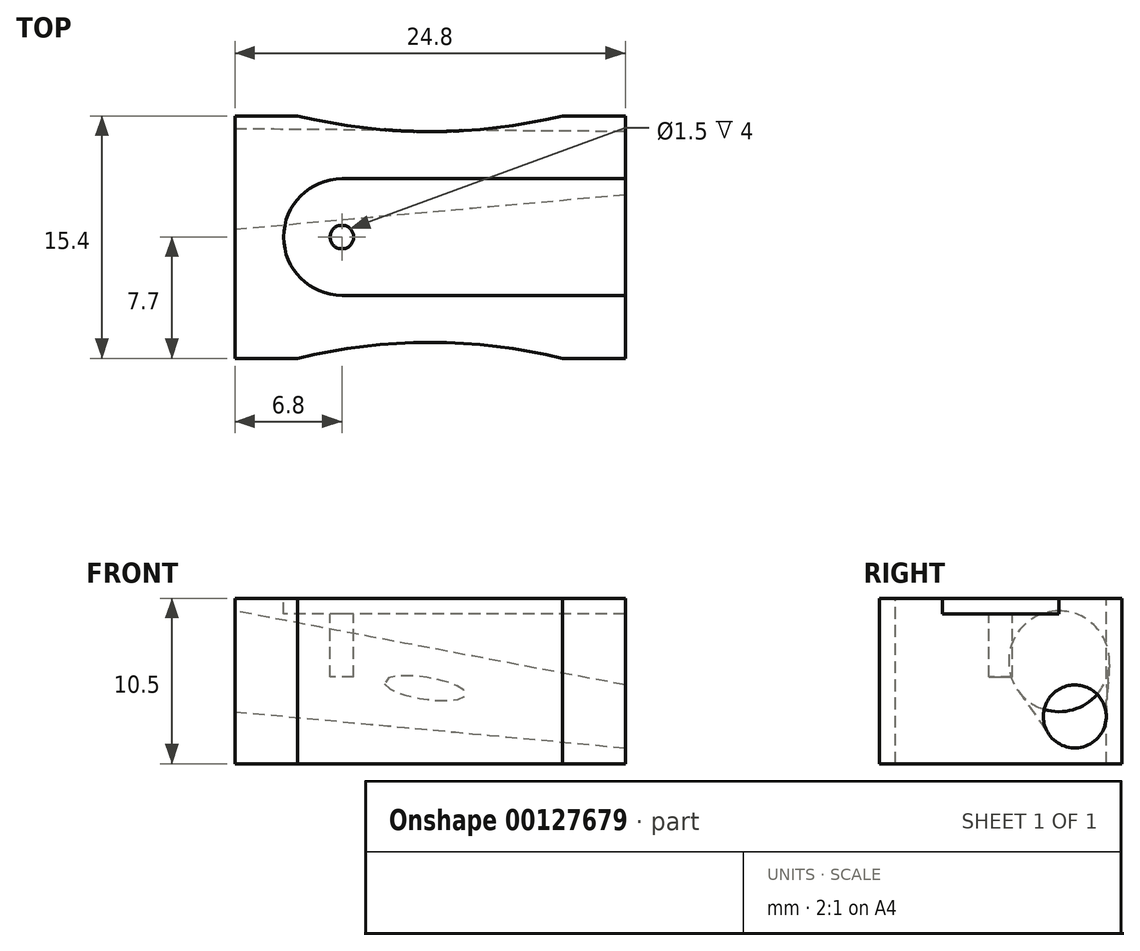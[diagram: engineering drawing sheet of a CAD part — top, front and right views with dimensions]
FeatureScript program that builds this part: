
annotation { "Feature Type Name" : "Feature", "Feature Type Description" : "" }
export const myFeature = defineFeature(function(context is Context, id is Id, definition is map)
    precondition{}
    {
        {
            var Q0;
            Q0=qCreatedBy(makeId("Top.planeOp"),FACE);
            var sketch = newSketch(context, id + "F0", { "sketchPlane" : qUnion([Q0])});
            skLineSegment(sketch, "E0.bottom", {"start": v(0, 0) * mm, "end": v(24.8, 0) * mm});
            skLineSegment(sketch, "E0.top", {"start": v(0, 15.4) * mm, "end": v(24.8, 15.4) * mm});
            skLineSegment(sketch, "E0.left", {"start": v(0, 0) * mm, "end": v(0, 15.4) * mm});
            skLineSegment(sketch, "E0.right", {"start": v(24.8, 0) * mm, "end": v(24.8, 15.4) * mm});
            skSolve(sketch);
        }
        {
            var Q0;
            Q0=makeQuery(id+"F0.imprint","IMPRINT",FACE,{"disambiguationData":[TD([[makeQuery(id+"F0.imprint","IMPRINT",EDGE,{"derivedFrom":sQuery(id+"F0.wireOp",EDGE,"E0.bottom")}),1.0]])]});
            extrude(context, id + "F1", {"entities" : qUnion([Q0]), "depth" : 10.5 * mm});
        }
        {
            var Q0;
            Q0=makeQuery(id+"F1.opExtrude","CAP_FACE",FACE,{"disambiguationData":[OSD([sQuery(id+"F0.wireOp",EDGE,"E0.bottom"),sQuery(id+"F0.wireOp",EDGE,"E0.top"),sQuery(id+"F0.wireOp",EDGE,"E0.left"),sQuery(id+"F0.wireOp",EDGE,"E0.right")])],"isStart":false});
            var sketch = newSketch(context, id + "F2", { "sketchPlane" : qUnion([Q0])});
            skLineSegment(sketch, "E1", {"start": v(24.8, 11.4) * mm, "end": v(6.8, 11.4) * mm});
            skLineSegment(sketch, "E2", {"start": v(24.8, 4) * mm, "end": v(6.8, 4) * mm});
            skArc(sketch, "E3", {"start": v(6.8, 11.4) * mm, "mid": v(3.1, 7.7) * mm, "end": v(6.8, 4) * mm});
            skSolve(sketch);
        }
        {
            var Q0;
            {var subQ0=sQuery(id+"F2.wireOp",EDGE,"E1");Q0=makeQuery(id+"F2.imprint","IMPRINT",FACE,{"disambiguationData":[TD([[makeQuery(id+"F2.imprint","IMPRINT",EDGE,{"derivedFrom":subQ0}),1.0]])]});}
            extrude(context, id + "F3", {"entities" : qUnion([Q0]), "operationType" : NewBodyOperationType.REMOVE, "oppositeDirection" : true, "depth" : 1 * mm});
        }
        {
            var Q0;
            Q0=makeQuery(id+"F1.opExtrude","CAP_FACE",FACE,{"disambiguationData":[OSD([sQuery(id+"F0.wireOp",EDGE,"E0.bottom"),sQuery(id+"F0.wireOp",EDGE,"E0.top"),sQuery(id+"F0.wireOp",EDGE,"E0.left"),sQuery(id+"F0.wireOp",EDGE,"E0.right")])],"isStart":false});
            var sketch = newSketch(context, id + "F4", { "sketchPlane" : qUnion([Q0])});
            skArc(sketch, "E4", {"start": v(4, 15.4) * mm, "mid": v(12.4, 14.4) * mm, "end": v(20.8, 15.4) * mm});
            skArc(sketch, "E5", {"start": v(20.8, 0) * mm, "mid": v(12.4, 1) * mm, "end": v(4, 0) * mm});
            skSolve(sketch);
        }
        {
            var Q0;
            {var subQ0=sQuery(id+"F4.wireOp",EDGE,"E4");Q0=makeQuery(id+"F4.imprint","IMPRINT",FACE,{"disambiguationData":[TD([[makeQuery(id+"F4.imprint","IMPRINT",EDGE,{"derivedFrom":subQ0}),1.0]])]});}
            var Q1;
            {var subQ0=sQuery(id+"F4.wireOp",EDGE,"E5");Q1=makeQuery(id+"F4.imprint","IMPRINT",FACE,{"disambiguationData":[TD([[makeQuery(id+"F4.imprint","IMPRINT",EDGE,{"derivedFrom":subQ0}),1.0]])]});}
            extrude(context, id + "F5", {"entities" : qUnion([Q0, Q1]), "operationType" : NewBodyOperationType.REMOVE, "oppositeDirection" : true, "depth" : 25 * mm});
        }
        {
            var Q0;
            Q0=makeQuery(id+"F1.opExtrude","SWEPT_FACE",FACE,{"disambiguationData":[OSD([sQuery(id+"F0.wireOp",EDGE,"E0.left")])]});
            var sketch = newSketch(context, id + "F6", { "sketchPlane" : qUnion([Q0])});
            skCircle(sketch, "E6", {"center": v(-11.4, 6.5) * mm, "radius": 3.2 * mm});
            skSolve(sketch);
        }
        {
            var Q0;
            Q0=makeQuery(id+"F1.opExtrude","SWEPT_FACE",FACE,{"disambiguationData":[OSD([sQuery(id+"F0.wireOp",EDGE,"E0.right")])]});
            var sketch = newSketch(context, id + "F7", { "sketchPlane" : qUnion([Q0])});
            skCircle(sketch, "E7", {"center": v(12.4, 3) * mm, "radius": 2 * mm});
            skSolve(sketch);
        }
        {
            var Q1;
            Q1=makeQuery(id+"F6.imprint","IMPRINT",FACE,{"disambiguationData":[TD([[makeQuery(id+"F6.imprint","IMPRINT",EDGE,{"derivedFrom":sQuery(id+"F6.wireOp",EDGE,"E6")}),1.0]])]});
            var Q2;
            Q2=makeQuery(id+"F7.imprint","IMPRINT",FACE,{"disambiguationData":[TD([[makeQuery(id+"F7.imprint","IMPRINT",EDGE,{"derivedFrom":sQuery(id+"F7.wireOp",EDGE,"E7")}),1.0]])]});
            loft(context, id + "F8", {"operationType" : NewBodyOperationType.REMOVE, "sheetProfilesArray" : [{ "sheetProfileEntities" : qUnion([Q1]) }, { "sheetProfileEntities" : qUnion([Q2]) }]});
        }
        {
            var Q0;
            Q0=makeQuery(id+"F3.boolean.opBoolean","COPY",FACE,{"derivedFrom":makeQuery(id+"F3.opExtrude","CAP_FACE",FACE,{"disambiguationData":[OSD([sQuery(id+"F0.wireOp",EDGE,"E0.right"),sQuery(id+"F2.wireOp",EDGE,"E1"),sQuery(id+"F2.wireOp",EDGE,"E2"),sQuery(id+"F2.wireOp",EDGE,"E3")])],"isStart":false})});
            var sketch = newSketch(context, id + "F9", { "sketchPlane" : qUnion([Q0])});
            skCircle(sketch, "E8", {"center": v(6.8, 7.7) * mm, "radius": 0.75 * mm});
            skSolve(sketch);
        }
        {
            var Q0;
            Q0=makeQuery(id+"F9.imprint","IMPRINT",FACE,{"disambiguationData":[TD([[makeQuery(id+"F9.imprint","IMPRINT",EDGE,{"derivedFrom":sQuery(id+"F9.wireOp",EDGE,"E8")}),1.0]])]});
            var Q1;
            Q1=sQuery(id+"F9.wireOp",EDGE,"E8");
            extrude(context, id + "F10", {"entities" : qUnion([Q0]), "operationType" : NewBodyOperationType.REMOVE, "surfaceEntities" : qUnion([Q1]), "oppositeDirection" : true, "depth" : 4 * mm});
        }
    });
